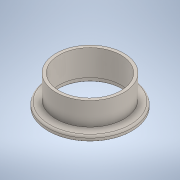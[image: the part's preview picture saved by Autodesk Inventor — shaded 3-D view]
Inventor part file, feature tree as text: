
AUTODESK INVENTOR PART (.ipt)
format: ipt  version: 2021 (Build 250183000, 183)  size: 148,480 bytes
history: native  units: in
note: dims shown in document units (in); Inventor stores cm internally (conversion verified against a paired STEP export)
features: extrude x1, sketch x1, chamfer x1
ambient origin geometry x8: Origin, YZ Plane, XZ Plane, XY Plane, X Axis, Y Axis, Z Axis, Center Point
bodies: Solid1 (feature_tree)
feature tree (3):
  extrude  "Extrusion3"  [1 undecoded]
  sketch  "Sketch3"  dims[d5=0.4134in d6=0.0in]
  chamfer  "Chamfer2"  [1 undecoded]
note: 2 required parameter values undecoded (feature->parameter linkage not recoverable at this tier; creation-order binding heuristic only, values carry confidence <= 0.55)
